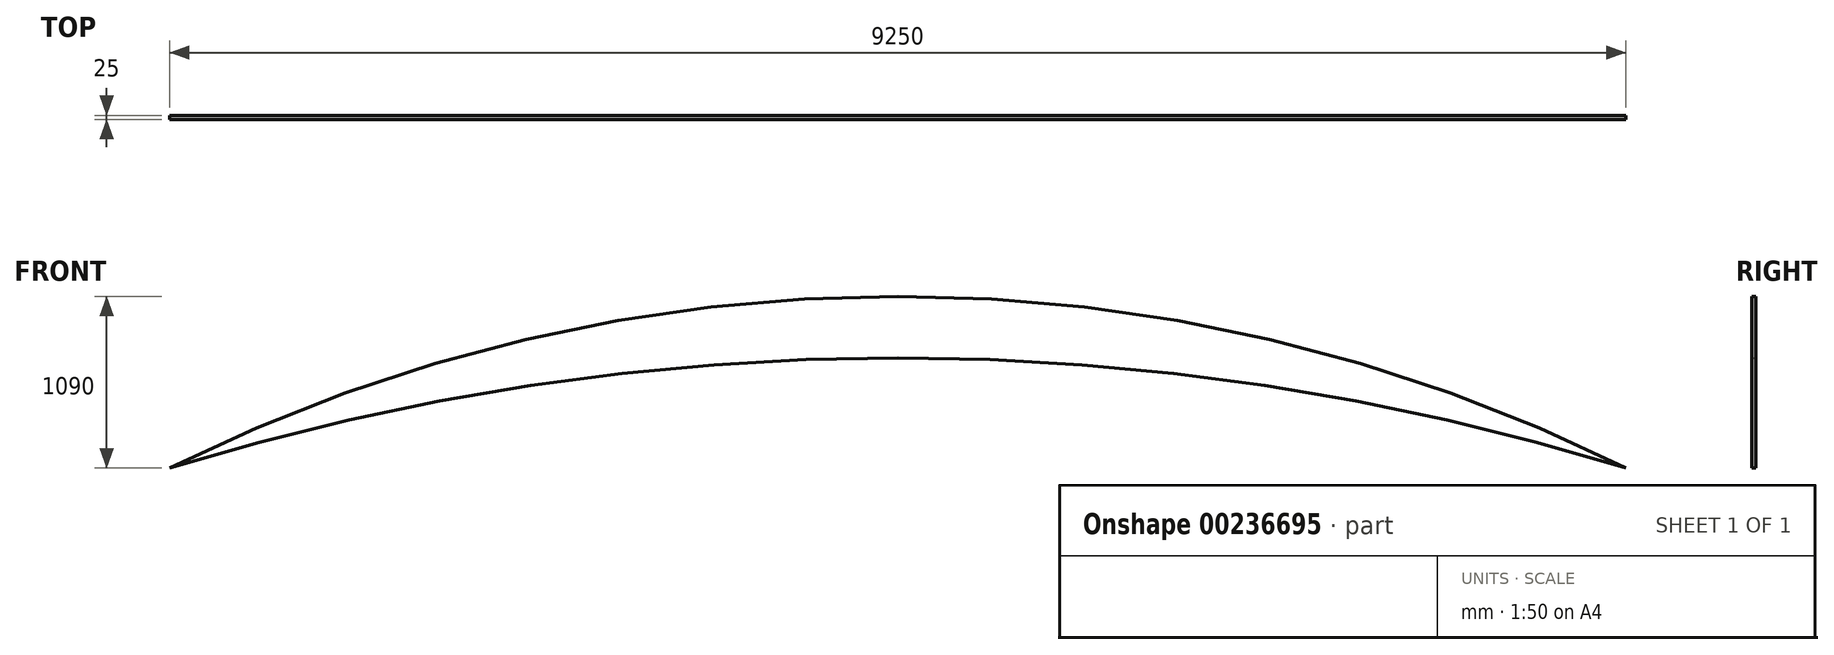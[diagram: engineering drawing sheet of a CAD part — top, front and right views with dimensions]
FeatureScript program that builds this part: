
annotation { "Feature Type Name" : "Feature", "Feature Type Description" : "" }
export const myFeature = defineFeature(function(context is Context, id is Id, definition is map)
    precondition{}
    {
        {
            var Q0;
            Q0=qCreatedBy(makeId("Front.planeOp"),FACE);
            var sketch = newSketch(context, id + "F0", { "sketchPlane" : qUnion([Q0])});
            skLineSegment(sketch, "E0", {"start": v(0, 0) * mm, "end": v(9250, 0) * mm, "construction": true});
            skArc(sketch, "E1", {"start": v(9250, 0) * mm, "mid": v(4625, 700) * mm, "end": v(0, 0) * mm});
            skArc(sketch, "E2", {"start": v(9250, 0) * mm, "mid": v(4625, 1090) * mm, "end": v(0, 0) * mm});
            skLineSegment(sketch, "E3", {"start": v(0, 0) * mm, "end": v(4625, -14929.02) * mm, "construction": true});
            skLineSegment(sketch, "E4", {"start": v(9250, 0) * mm, "end": v(4625, -14929.02) * mm, "construction": true});
            skLineSegment(sketch, "E5", {"start": v(4625, -9267.21) * mm, "end": v(9250, 0) * mm, "construction": true});
            skLineSegment(sketch, "E6", {"start": v(4625, -9267.21) * mm, "end": v(0, 0) * mm, "construction": true});
            skSolve(sketch);
        }
        {
            var Q0;
            Q0=makeQuery(id+"F0.imprint","IMPRINT",FACE,{"disambiguationData":[TD([[makeQuery(id+"F0.imprint","IMPRINT",EDGE,{"derivedFrom":sQuery(id+"F0.wireOp",EDGE,"E1")}),-1.0]])]});
            extrude(context, id + "F1", {"entities" : qUnion([Q0]), "depth" : 25 * mm, "offsetDistance" : 25 * mm});
        }
    });
